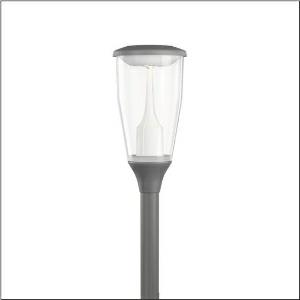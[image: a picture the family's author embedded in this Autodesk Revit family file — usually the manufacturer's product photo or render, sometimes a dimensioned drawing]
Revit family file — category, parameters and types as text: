
# Revit family: dl_11_iq___st1_2a_5xa5565mf14hp00022_149f
name_source: partatom
category: Lighting Fixtures
units: mm (PartAtom-declared; Revit-internal decimal feet)

## family parameters
Cut with Voids When Loaded = No
Host = Face
Light Source = No
Part Type = Normal
Room Calculation Point = No
Round Connector Dimension = Use Diameter
Shared = No

## types (1)
- --- (1 x LED, 4340 lm, 33.6 W, 2700K)
    Apparent Load = 34 VA
    CIE Flux Codes = 23 60 93 95 100
    Color Rendering = 70
    Color Temperature = 2700K
    Default Elevation = 1800 mm
    Description = DL 11 iQ, mast luminaire, Module 540 iQ-SR, primary light control with 3 zone facetted reflector, of plastic, silver coated, highly specular, structured, primary optical cover: cover, of PMMA, transparent, light distribution: ST1.2a, light emission: direct distribution, primary light characteristic: asymmetric, installation type: post-top, LED, High Power LED, light colour: 727, colour temperature: 2700K, control gear: iQ Street-Remote, control: Street-Remote, Auto-Match, Temp-Guard, Lumen-Switch, Night-Set, Smart-Wire, Light-Fading, Desk-Remote (wireless, voltage-free reading and setting of iQ features in the workshop via application-optimized NFC function/RFID function), optimised constant luminous flux control (CLO 2.0), mains connection: 220..240V, AC, 50/60Hz, connection cable pre-assembled, cable length: 5,5m, start of lifetime: 34W, end of service life: 36W, luminaire housing, upper part, of diecast aluminium, coated, SITECO metallic grey (DB 702S), spigot size: 60mm (post-top), mounting height: 3..5m, post-top mast mounting element, of diecast aluminium, coated, SITECO metallic grey (DB 702S), Module 540 iQ-SR, traffic white (RAL 9016), equipment: Power, protection rating (complete): IP66, insulation class (complete): insulation class II (safety insulation), certification: CE, ENEC, ENEC+, VDE, impact resistance: IK07, packaging unit: 1 piece

Light Distribution: ST1.2a
    Height = 665 mm
    Lamp = 1 x LED
    Lamp Light Flux = 4340 lm
    Lamp Power = 33.6 W
    Lamp count = 1
    Length = 334 mm
    Luminous efficacy = 129 lm/W
    Manufacturer = Siteco
    ModVariant = No
    Model = 5XA5565MF14HP00022
    Number of Poles = 1
    OnlyDefault = Yes
    Power Factor = 1
    Product Name = DL 11 iQ | ST1.2a
    Product group = mast luminaire | pylon top
    ProductGroupID = 6100
    Protection Class = Protection class II
    Protection Degree = IP 66
    RLX_Detail_Level = 1
    RLX_Emergency_Light_Flux = 0 lm
    RLX_Emergency_Type = 0
    RLX_Emergency_Type_DB = No
    RlxData = <blob elided: 155925 chars, md5=10b83d32>
    Socket = socket
    Standby Power = 0 W
    System Light Flux = 4340 lm
    System Power = 34 W
    Type Comments = factory setting: luminous flux: 100 % | dim-lin: 254 | 695 mA
    Type Image = l_1258354.jpg
    URL = http://relux.com
    VarID = @adj_040235
    Voltage = 0 V
    Weight = 0.00 kg
    Width = 0 mm  [stored 0 ft]

note: [stored X ft] marks values corroborated as IEEE doubles in the binary element streams (Revit-internal decimal feet)

## geometry (parser evidence)
native form markers: Blend x4, Sweep x9
no freeform markers — native parametric forms only
